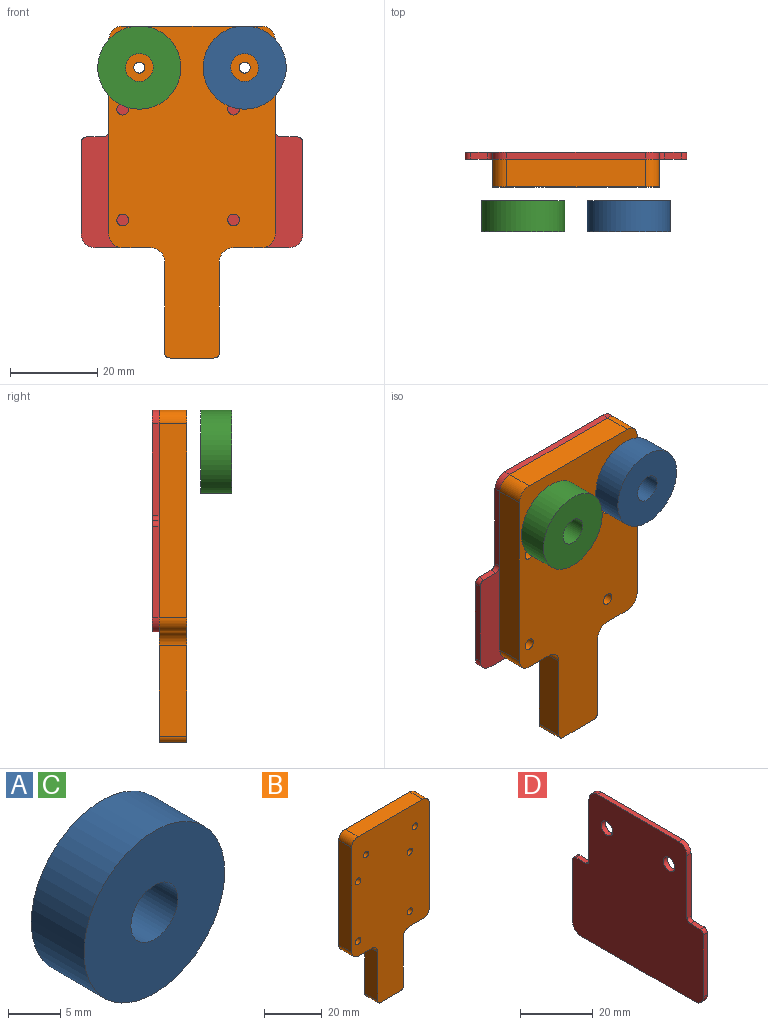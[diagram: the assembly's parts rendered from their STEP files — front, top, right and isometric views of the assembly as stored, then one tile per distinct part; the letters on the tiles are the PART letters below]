
ASSEMBLY  parts=4 mates=3
PART A: 4 faces, bbox 19.1x7.1x19.1 mm
  f0: cylinder r=3.17mm len=7.14mm, axis (0,1,0), area 142.4mm2, adj f2,f3
  f1: cylinder r=9.53mm len=19.05mm, axis (0,1,0), area 427.2mm2, adj f2,f3
  f2: plane 19.05x19.05mm, normal (0,-1,0), area 253.4mm2, adj f0,f1
  f3: plane 19.05x19.05mm, normal (0,1,0), area 253.4mm2, adj f0,f1
PART B: 24 faces, bbox 38.1x6.4x76.1 mm
  f0: cylinder r=3.17mm len=6.35mm, axis (0,1,0), area 31.7mm2, adj f1,f15,f16,f17
  f1: plane 6.41x6.35mm, normal (0,0,-1), area 40.7mm2, adj f0,f2,f16,f17
  f2: cylinder r=3.17mm len=6.35mm, axis (0,1,0), area 31.7mm2, adj f1,f3,f16,f17
  f3: plane 44.45x6.35mm, normal (1,0,0), area 282.3mm2, adj f2,f4,f16,f17
  f4: cylinder r=3.17mm len=6.35mm, axis (0,1,0), area 31.7mm2, adj f3,f5,f16,f17
  f5: plane 31.75x6.35mm, normal (0,0,1), area 201.6mm2, adj f4,f6,f16,f17
  f6: cylinder r=3.17mm len=6.35mm, axis (0,1,0), area 31.7mm2, adj f5,f7,f16,f17
  f7: plane 44.45x6.35mm, normal (-1,0,0), area 282.3mm2, adj f6,f8,f16,f17
  f8: cylinder r=3.17mm len=6.35mm, axis (0,1,0), area 31.7mm2, adj f7,f9,f16,f17
  f9: plane 6.41x6.35mm, normal (0,0,-1), area 40.7mm2, adj f8,f10,f16,f17
  f10: cylinder r=3.17mm len=6.35mm, axis (0,1,0), area 31.7mm2, adj f9,f11,f16,f17
  f11: plane 20.83x6.35mm, normal (-1,0,0), area 132.3mm2, adj f10,f12,f16,f17
  f12: cylinder r=1.27mm len=6.35mm, axis (0,1,0), area 12.7mm2, adj f11,f13,f16,f17
  f13: plane 10.03x6.35mm, normal (0,0,-1), area 63.7mm2, adj f12,f14,f16,f17
  f14: cylinder r=1.27mm len=6.35mm, axis (0,1,0), area 12.7mm2, adj f13,f15,f16,f17
  f15: plane 20.83x6.35mm, normal (1,0,0), area 132.3mm2, adj f0,f14,f16,f17
  f16: plane 76.07x38.1mm, normal (0,-1,0), area 2215.1mm2, adj f0,f1,f2,f3,f4,f5,f6,f7
  f17: plane 76.07x38.1mm, normal (0,1,0), area 2215.1mm2, adj f0,f1,f2,f3,f4,f5,f6,f7
  f18: cylinder r=1.27mm len=6.35mm, axis (0,1,0), area 50.7mm2, adj f16,f17
  f19: cylinder r=1.27mm len=6.35mm, axis (0,1,0), area 50.7mm2, adj f16,f17
  f20: cylinder r=1.35mm len=6.35mm, axis (0,-1,0), area 54mm2, adj f16,f17
  f21: cylinder r=1.35mm len=6.35mm, axis (0,-1,0), area 54mm2, adj f16,f17
  f22: cylinder r=1.35mm len=6.35mm, axis (0,-1,0), area 54mm2, adj f16,f17
  f23: cylinder r=1.35mm len=6.35mm, axis (0,-1,0), area 54mm2, adj f16,f17
PART C: same geometry as A
PART D: 20 faces, bbox 1.6x50.8x50.8 mm
  f0: plane 20.96x1.59mm, normal (0,1,0), area 33.3mm2, adj f1,f15,f16,f17
  f1: cylinder r=3.17mm len=3.18mm, axis (-1,0,0), area 7.9mm2, adj f0,f2,f16,f17
  f2: plane 31.75x1.59mm, normal (0,0,1), area 50.4mm2, adj f1,f3,f16,f17
  f3: cylinder r=3.17mm len=3.18mm, axis (-1,0,0), area 7.9mm2, adj f2,f4,f16,f17
  f4: plane 20.96x1.59mm, normal (0,-1,0), area 33.3mm2, adj f3,f5,f16,f17
  f5: cylinder r=1.27mm len=1.59mm, axis (-1,0,0), area 3.2mm2, adj f4,f6,f16,f17
  f6: plane 3.81x1.59mm, normal (0,0,1), area 6mm2, adj f5,f7,f16,f17
  f7: cylinder r=1.27mm len=1.59mm, axis (-1,0,0), area 3.2mm2, adj f6,f8,f16,f17
  f8: plane 20.96x1.59mm, normal (0,-1,0), area 33.3mm2, adj f7,f9,f16,f17
  f9: cylinder r=3.17mm len=3.18mm, axis (-1,0,0), area 7.9mm2, adj f8,f10,f16,f17
  f10: plane 44.45x1.59mm, normal (0,0,-1), area 70.6mm2, adj f9,f11,f16,f17
  f11: cylinder r=3.17mm len=3.18mm, axis (-1,0,0), area 7.9mm2, adj f10,f12,f16,f17
  f12: plane 20.96x1.59mm, normal (0,1,0), area 33.3mm2, adj f11,f13,f16,f17
  f13: cylinder r=1.27mm len=1.59mm, axis (-1,0,0), area 3.2mm2, adj f12,f14,f16,f17
  f14: plane 3.81x1.59mm, normal (0,0,1), area 6mm2, adj f13,f15,f16,f17
  f15: cylinder r=1.27mm len=1.59mm, axis (-1,0,0), area 3.2mm2, adj f0,f14,f16,f17
  f16: plane 50.8x50.8mm, normal (1,0,0), area 2217.7mm2, adj f0,f1,f2,f3,f4,f5,f6,f7
  f17: plane 50.8x50.8mm, normal (-1,0,0), area 2217.7mm2, adj f0,f1,f2,f3,f4,f5,f6,f7
  f18: cylinder r=2.25mm len=4.5mm, axis (1,0,0), area 22.4mm2, adj f16,f17
  f19: cylinder r=2.25mm len=4.5mm, axis (1,0,0), area 22.4mm2, adj f16,f17
PLACE A t=(12.06,-6.35,66.55)mm
PLACE B t=(0,3.18,50.67)mm
PLACE C t=(-12.06,-6.35,66.55)mm
PLACE D rot(axis=(0,0,-1),90deg) t=(0,4.76,50.67)mm
MATE fastened B.f18 <-> A.f0  axis (0,-1,0) through (12.06,-3.17,66.55)mm
MATE fastened C.f0 <-> B.f19  axis (0,1,0) through (-12.06,-6.35,66.55)mm
MATE fastened B.f19 <-> D.f19  axis (0,1,0) through (-12.06,3.18,66.55)mm
